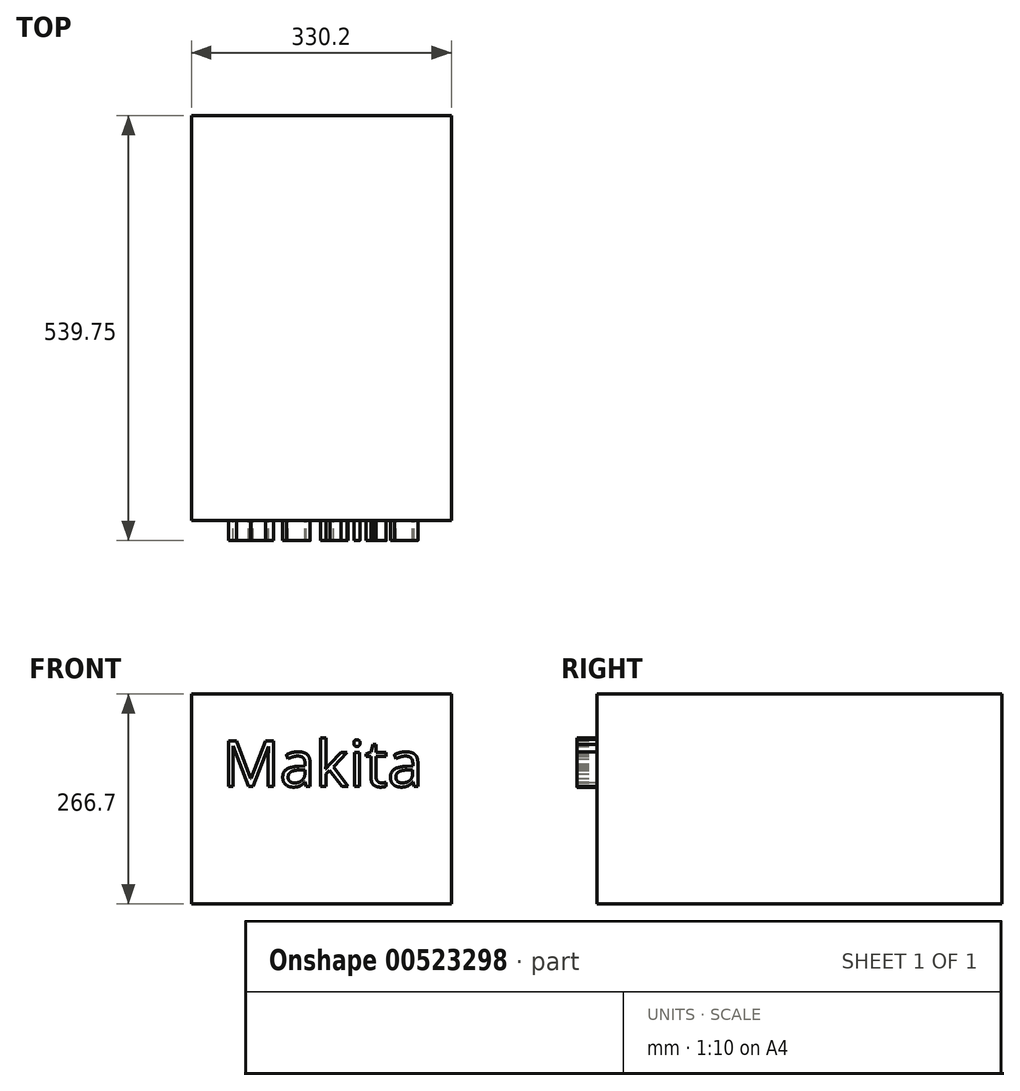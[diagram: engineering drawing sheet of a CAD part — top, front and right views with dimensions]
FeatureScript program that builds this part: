
annotation { "Feature Type Name" : "Feature", "Feature Type Description" : "" }
export const myFeature = defineFeature(function(context is Context, id is Id, definition is map)
    precondition{}
    {
        {
            var Q0;
            Q0=qCreatedBy(makeId("Front.planeOp"),FACE);
            var sketch = newSketch(context, id + "F0", { "sketchPlane" : qUnion([Q0])});
            skLineSegment(sketch, "E0.bottom", {"start": v(165.1, 133.35) * mm, "end": v(-165.1, 133.35) * mm});
            skLineSegment(sketch, "E0.top", {"start": v(165.1, -133.35) * mm, "end": v(-165.1, -133.35) * mm});
            skLineSegment(sketch, "E0.left", {"start": v(165.1, 133.35) * mm, "end": v(165.1, -133.35) * mm});
            skLineSegment(sketch, "E0.right", {"start": v(-165.1, 133.35) * mm, "end": v(-165.1, -133.35) * mm});
            skPoint(sketch, "E0.middle", {"position": v(0, 0) * mm});
            skSolve(sketch);
        }
        {
            var Q0;
            Q0=makeQuery(id+"F0.imprint","IMPRINT",FACE,{"disambiguationData":[TD([[makeQuery(id+"F0.imprint","IMPRINT",EDGE,{"derivedFrom":sQuery(id+"F0.wireOp",EDGE,"E0.bottom")}),1.0]])]});
            extrude(context, id + "F1", {"entities" : qUnion([Q0]), "depth" : 514.35 * mm, "offsetDistance" : 25.4 * mm});
        }
        {
            var Q0;
            Q0=makeQuery(id+"F1.opExtrude","CAP_FACE",FACE,{"disambiguationData":[OSD([sQuery(id+"F0.wireOp",EDGE,"E0.bottom"),sQuery(id+"F0.wireOp",EDGE,"E0.top"),sQuery(id+"F0.wireOp",EDGE,"E0.left"),sQuery(id+"F0.wireOp",EDGE,"E0.right")])],"isStart":false});
            var sketch = newSketch(context, id + "F2", { "sketchPlane" : qUnion([Q0])});
            skText(sketch, "E1", { "text": "Makita", "fontName": "OpenSans-Regular.ttf"});
            const initialGuessF2  = {"E1": [-0.126, 0.01574, 1, 0, 0.05843]};
            skSetInitialGuess(sketch, initialGuessF2);
            skSolve(sketch);
        }
        {
            var Q0;
            Q0 = qSketchRegion(id + "F2", true);
            extrude(context, id + "F3", {"entities" : qUnion([Q0]), "operationType" : NewBodyOperationType.ADD, "depth" : 25.4 * mm, "offsetDistance" : 25.4 * mm});
        }
    });
